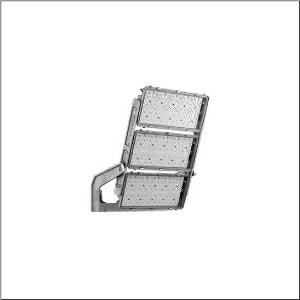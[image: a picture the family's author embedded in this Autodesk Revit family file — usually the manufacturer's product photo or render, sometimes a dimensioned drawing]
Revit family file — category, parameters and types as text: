
# Revit family: floodlight_fl_11_maxi_pro_remote___pl33tblc_5xa779426h01aa_354a
name_source: partatom
category: Lighting Fixtures
units: mm (PartAtom-declared; Revit-internal decimal feet)

## family parameters
Cut with Voids When Loaded = No
Host = Face
Light Source = No
Part Type = Normal
Room Calculation Point = No
Round Connector Dimension = Use Diameter
Shared = No

## types (1)
- --- (1 x LED, 124720 lm, 1388.3 W, 4000K)
    Apparent Load = 1388 VA
    CIE Flux Codes = 24 77 100 100 100
    Color Rendering = 70
    Color Temperature = 4000K
    Default Elevation = 1800 mm
    Description = Floodlight FL 11  maxi  pro Remote floodlight; light control with lens of PMMA; cover panel of toughened safety glass, transparent; light distribution: PL33TBLC, asymmetric direct distribution, LEDcolour temperature: 4000K, rated luminous flux: 124.720lm, colour rendering: CRI > 70, light colour: 740; luminous efficacy: 90lm/W; brightness control: DALI 2 (1 DALI address); with terminal, 8-pole, max. 2.5mm², mains connection: 220..240V/380..400V AC, 50/60Hz, surge voltage resistance: line to ground: 10kV, ECG replaceable separately, LED unit replaceable without ESD environment, dustproof LED module, dimming range 10..100%, no afterglow with DALI off / DMX off command; 1388W floodlight with 2x LED unit of diecast aluminium, coated grey; length: 713mm / width: 651mm / height: 338mm; mounting bracket, of diecast aluminium, uncoated, natural, equipment: Power, protection rating (complete): IP66; insulation class (complete): insulation class I (protective earthing); certification: CE, ENEC, VDE; ball protection: ball impact resistance with accessories, impact resistance: IK07; rated ambient temperature 10°C, only for outdoor installations, permissible operating ambient temperature: -40..+30°C, permissible storage temperature: -40..+85°Cpackaging unit: 1 piece

Light Distribution: PL33TBLC
    Height = 320 mm
    Lamp = 1 x LED
    Lamp Light Flux = 124720 lm
    Lamp Power = 1388.3 W
    Lamp count = 1
    Length = 1002 mm
    Luminous efficacy = 90 lm/W
    Manufacturer = Siteco
    ModVariant = No
    Model = 5XA779426H01AA
    Mounting Place = Ceiling
    Mounting Type = Surface mounted
    Number of Poles = 1
    OnlyDefault = Yes
    Power Factor = 1
    Product Name = Floodlight FL 11 maxi pro Remote | PL33TBLC
    Product group = floodlight | ceiling mounted
    ProductGroupID = 301
    Protection Class = Protection class I
    Protection Degree = IP 66
    RLX_Detail_Level = 1
    RLX_Emergency_Light_Flux = 0 lm
    RLX_Emergency_Type = 0
    RLX_Emergency_Type_DB = No
    RlxData = <blob elided: 52025 chars, md5=967a7894>
    Socket = socket
    Standby Power = 0 W
    System Light Flux = 124720 lm
    System Power = 1388 W
    Type Comments = factory setting: luminous flux: 100 % | dim-lin: 254 | 955 mA
    Type Image = l_1349141.jpg
    URL = http://relux.com
    VarID = @adj_096008
    Voltage = 0 V
    Weight = 0.00 kg
    Width = 655 mm

## geometry (parser evidence)
native form markers: Blend x4, Sweep x11
no freeform markers — native parametric forms only
